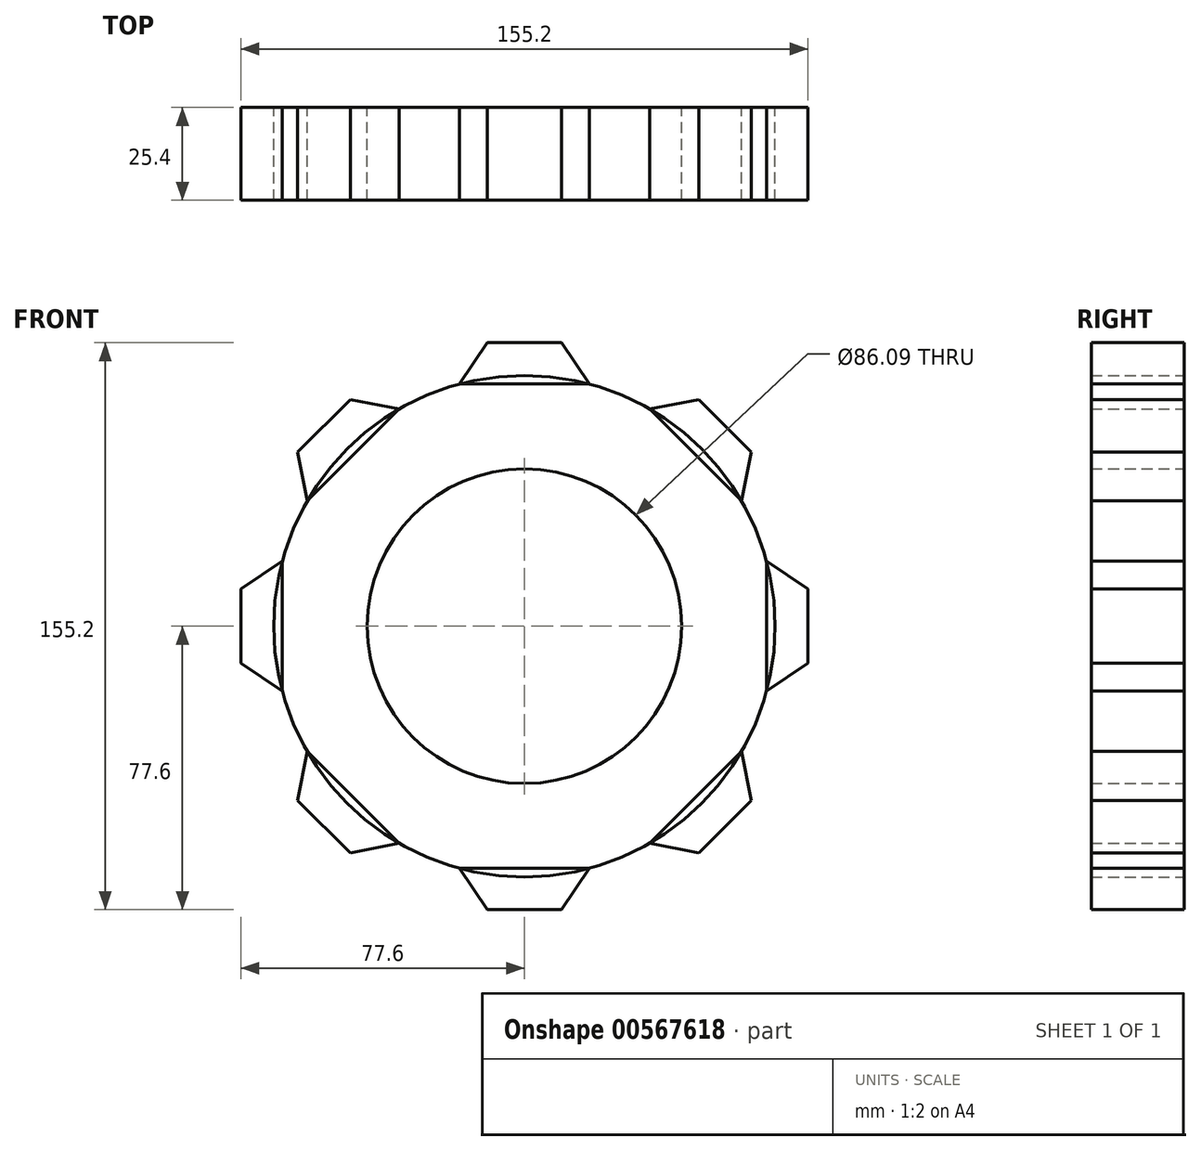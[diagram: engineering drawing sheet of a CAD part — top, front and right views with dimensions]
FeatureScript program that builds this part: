
annotation { "Feature Type Name" : "Feature", "Feature Type Description" : "" }
export const myFeature = defineFeature(function(context is Context, id is Id, definition is map)
    precondition{}
    {
        {
            var Q0;
            Q0=qCreatedBy(makeId("Front.planeOp"),FACE);
            var sketch = newSketch(context, id + "F0", { "sketchPlane" : qUnion([Q0])});
            skCircle(sketch, "E0", {"center": v(0, 0) * mm, "radius": 68.62 * mm});
            skCircle(sketch, "E1", {"center": v(0, 0) * mm, "radius": 43.05 * mm});
            skSolve(sketch);
        }
        {
            var Q0;
            Q0=makeQuery(id+"F0.imprint","IMPRINT",FACE,{"disambiguationData":[TD([[makeQuery(id+"F0.imprint","IMPRINT",EDGE,{"derivedFrom":sQuery(id+"F0.wireOp",EDGE,"E0")}),1.0]])]});
            extrude(context, id + "F1", {"entities" : qUnion([Q0]), "depth" : 25.4 * mm, "offsetDistance" : 25.4 * mm});
        }
        {
            var Q0;
            Q0=qCreatedBy(makeId("Front.planeOp"),FACE);
            var sketch = newSketch(context, id + "F2", { "sketchPlane" : qUnion([Q0])});
            skLineSegment(sketch, "E2.bottom", {"start": v(-10.16, 77.6) * mm, "end": v(10.16, 77.6) * mm});
            skLineSegment(sketch, "E2.top", {"start": v(-17.78, 66.28) * mm, "end": v(17.78, 66.28) * mm});
            skLineSegment(sketch, "E3", {"start": v(-10.16, 77.6) * mm, "end": v(-17.78, 66.28) * mm});
            skLineSegment(sketch, "E4", {"start": v(10.16, 77.6) * mm, "end": v(17.78, 66.28) * mm});
            skSolve(sketch);
        }
        {
            var Q0;
            Q0 = qSketchRegion(id + "F2", true);
            extrude(context, id + "F3", {"entities" : qUnion([Q0]), "depth" : 25.4 * mm, "offsetDistance" : 25.4 * mm});
        }
        {
            var Q0;
            Q0=qCreatedBy(makeId("Top.planeOp"),FACE);
            var sketch = newSketch(context, id + "F4", { "sketchPlane" : qUnion([Q0])});
            skLineSegment(sketch, "E5", {"start": v(0, -68.19) * mm, "end": v(0, 59.4) * mm});
            skSolve(sketch);
        }
        {
            var Q0;
            Q0=makeQuery(id+"F3.opExtrude","SWEPT_BODY",BODY,{"disambiguationData":[OSD([sQuery(id+"F2.wireOp",EDGE,"E2.bottom"),sQuery(id+"F2.wireOp",EDGE,"E2.top"),sQuery(id+"F2.wireOp",EDGE,"E3"),sQuery(id+"F2.wireOp",EDGE,"E4")])]});
            var Q1;
            Q1=sQuery(id+"F4.wireOp",EDGE,"E5");
            circularPattern(context, id + "F5", {"entities" : qUnion([Q0]), "axis" : qUnion([Q1]), "angle" : 360 * degree, "instanceCount" : 8, "equalSpace" : true});
        }
    });
